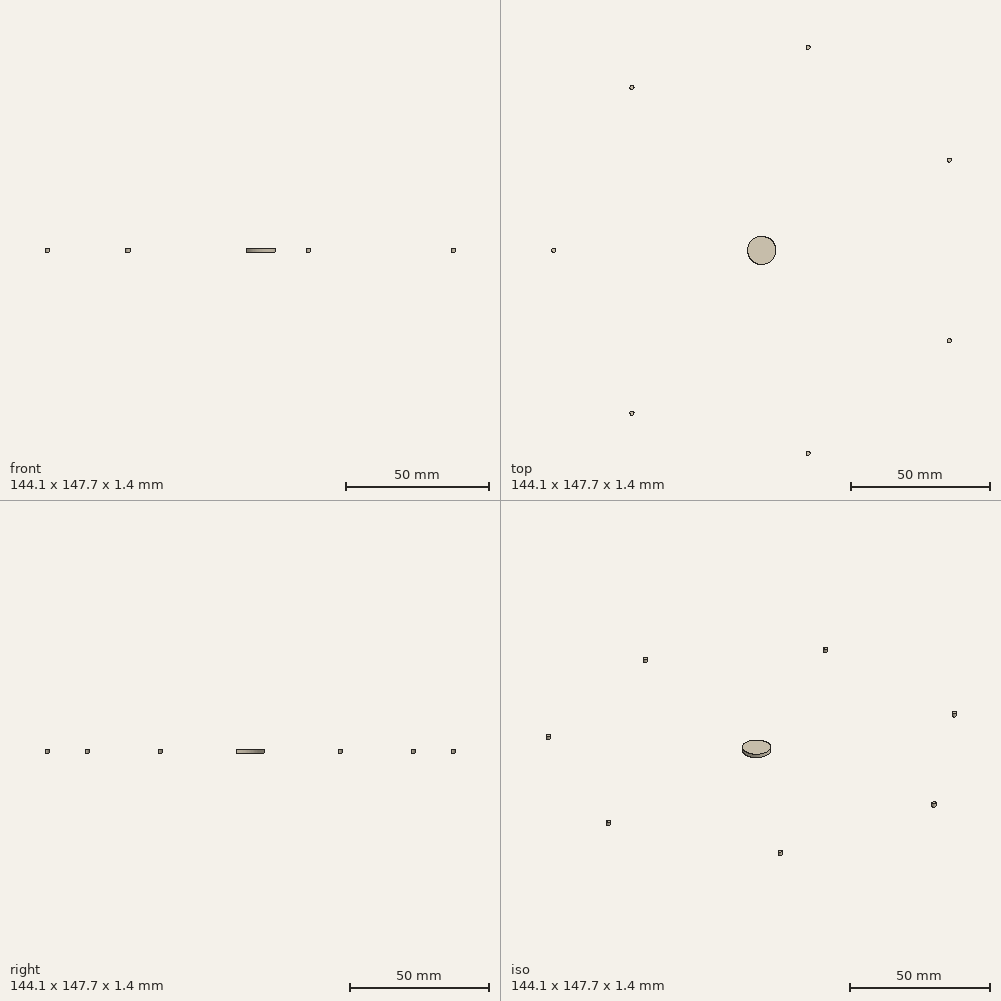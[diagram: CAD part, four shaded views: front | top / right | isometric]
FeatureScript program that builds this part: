
annotation { "Feature Type Name" : "Feature", "Feature Type Description" : "" }
export const myFeature = defineFeature(function(context is Context, id is Id, definition is map)
    precondition{}
    {
        {
            var Q0;
            Q0=qCreatedBy(makeId("Top.planeOp"),FACE);
            var sketch = newSketch(context, id + "F0", { "sketchPlane" : qUnion([Q0])});
            skLineSegment(sketch, "E0.0.left", {"start": v(-72.94, 1) * mm, "end": v(-5, 1) * mm});
            skLineSegment(sketch, "E0.0.right", {"start": v(-72.94, -1) * mm, "end": v(-5, -1) * mm});
            skCircle(sketch, "E1", {"center": v(-75, 0) * mm, "radius": 0.75 * mm});
            skArc(sketch, "E2", {"start": v(-74.31, 1.33) * mm, "mid": v(-76.5, 0) * mm, "end": v(-74.31, -1.33) * mm});
            skPoint(sketch, "E3.newPointA", {"position": v(-72.94, 1) * mm});
            skArc(sketch, "E3.filletArc", {"start": v(-74.31, 1.33) * mm, "mid": v(-73.65, 1.08) * mm, "end": v(-72.94, 1) * mm});
            skPoint(sketch, "E4.newPointB", {"position": v(-72.94, -1) * mm});
            skArc(sketch, "E4.filletArc", {"start": v(-72.94, -1) * mm, "mid": v(-73.65, -1.08) * mm, "end": v(-74.31, -1.33) * mm});
            skLineSegment(sketch, "E5.1.0", {"start": v(-46.26, -56.4) * mm, "end": v(-3.9, -3.29) * mm});
            skPoint(sketch, "E5.1.1", {"position": v(-44.7, -57.65) * mm});
            skPoint(sketch, "E5.1.2", {"position": v(-46.26, -56.4) * mm});
            skLineSegment(sketch, "E5.1.3", {"start": v(-44.7, -57.65) * mm, "end": v(-2.34, -4.53) * mm});
            skArc(sketch, "E5.1.4", {"start": v(-47.38, -57.27) * mm, "mid": v(-47.7, -59.81) * mm, "end": v(-45.3, -58.93) * mm});
            skCircle(sketch, "E5.1.5", {"center": v(-46.76, -58.64) * mm, "radius": 0.75 * mm});
            skArc(sketch, "E5.1.6", {"start": v(-44.7, -57.65) * mm, "mid": v(-45.07, -58.25) * mm, "end": v(-45.3, -58.93) * mm});
            skArc(sketch, "E5.1.7", {"start": v(-47.38, -57.27) * mm, "mid": v(-46.77, -56.9) * mm, "end": v(-46.26, -56.4) * mm});
            skLineSegment(sketch, "E5.2.0", {"start": v(15.26, -71.33) * mm, "end": v(0.14, -5.1) * mm});
            skPoint(sketch, "E5.2.1", {"position": v(17.2, -70.89) * mm});
            skPoint(sketch, "E5.2.2", {"position": v(15.26, -71.33) * mm});
            skLineSegment(sketch, "E5.2.3", {"start": v(17.2, -70.89) * mm, "end": v(2.09, -4.65) * mm});
            skArc(sketch, "E5.2.4", {"start": v(15.24, -72.75) * mm, "mid": v(17.02, -74.58) * mm, "end": v(17.84, -72.15) * mm});
            skCircle(sketch, "E5.2.5", {"center": v(16.69, -73.12) * mm, "radius": 0.75 * mm});
            skArc(sketch, "E5.2.6", {"start": v(17.2, -70.89) * mm, "mid": v(17.45, -71.56) * mm, "end": v(17.84, -72.15) * mm});
            skArc(sketch, "E5.2.7", {"start": v(15.24, -72.75) * mm, "mid": v(15.33, -72.04) * mm, "end": v(15.26, -71.33) * mm});
            skLineSegment(sketch, "E5.3.0", {"start": v(65.28, -32.55) * mm, "end": v(4.07, -3.07) * mm});
            skPoint(sketch, "E5.3.1", {"position": v(66.15, -30.75) * mm});
            skPoint(sketch, "E5.3.2", {"position": v(65.28, -32.55) * mm});
            skLineSegment(sketch, "E5.3.3", {"start": v(66.15, -30.75) * mm, "end": v(4.94, -1.27) * mm});
            skArc(sketch, "E5.3.4", {"start": v(66.38, -33.44) * mm, "mid": v(68.92, -33.2) * mm, "end": v(67.53, -31.04) * mm});
            skCircle(sketch, "E5.3.5", {"center": v(67.57, -32.54) * mm, "radius": 0.75 * mm});
            skArc(sketch, "E5.3.6", {"start": v(66.15, -30.75) * mm, "mid": v(66.82, -30.98) * mm, "end": v(67.53, -31.04) * mm});
            skArc(sketch, "E5.3.7", {"start": v(66.38, -33.44) * mm, "mid": v(65.88, -32.93) * mm, "end": v(65.28, -32.55) * mm});
            skLineSegment(sketch, "E5.4.0", {"start": v(66.15, 30.75) * mm, "end": v(4.94, 1.27) * mm});
            skPoint(sketch, "E5.4.1", {"position": v(65.28, 32.55) * mm});
            skPoint(sketch, "E5.4.2", {"position": v(66.15, 30.75) * mm});
            skLineSegment(sketch, "E5.4.3", {"start": v(65.28, 32.55) * mm, "end": v(4.07, 3.07) * mm});
            skArc(sketch, "E5.4.4", {"start": v(67.53, 31.04) * mm, "mid": v(68.92, 33.2) * mm, "end": v(66.38, 33.44) * mm});
            skCircle(sketch, "E5.4.5", {"center": v(67.57, 32.54) * mm, "radius": 0.75 * mm});
            skArc(sketch, "E5.4.6", {"start": v(65.28, 32.55) * mm, "mid": v(65.88, 32.93) * mm, "end": v(66.38, 33.44) * mm});
            skArc(sketch, "E5.4.7", {"start": v(67.53, 31.04) * mm, "mid": v(66.82, 30.98) * mm, "end": v(66.15, 30.75) * mm});
            skLineSegment(sketch, "E5.5.0", {"start": v(17.2, 70.89) * mm, "end": v(2.09, 4.65) * mm});
            skPoint(sketch, "E5.5.1", {"position": v(15.26, 71.33) * mm});
            skPoint(sketch, "E5.5.2", {"position": v(17.2, 70.89) * mm});
            skLineSegment(sketch, "E5.5.3", {"start": v(15.26, 71.33) * mm, "end": v(0.14, 5.1) * mm});
            skArc(sketch, "E5.5.4", {"start": v(17.84, 72.15) * mm, "mid": v(17.02, 74.58) * mm, "end": v(15.24, 72.75) * mm});
            skCircle(sketch, "E5.5.5", {"center": v(16.69, 73.12) * mm, "radius": 0.75 * mm});
            skArc(sketch, "E5.5.6", {"start": v(15.26, 71.33) * mm, "mid": v(15.33, 72.04) * mm, "end": v(15.24, 72.75) * mm});
            skArc(sketch, "E5.5.7", {"start": v(17.84, 72.15) * mm, "mid": v(17.45, 71.56) * mm, "end": v(17.2, 70.89) * mm});
            skLineSegment(sketch, "E5.6.0", {"start": v(-44.7, 57.65) * mm, "end": v(-2.34, 4.53) * mm});
            skPoint(sketch, "E5.6.1", {"position": v(-46.26, 56.4) * mm});
            skPoint(sketch, "E5.6.2", {"position": v(-44.7, 57.65) * mm});
            skLineSegment(sketch, "E5.6.3", {"start": v(-46.26, 56.4) * mm, "end": v(-3.9, 3.29) * mm});
            skArc(sketch, "E5.6.4", {"start": v(-45.3, 58.93) * mm, "mid": v(-47.7, 59.81) * mm, "end": v(-47.38, 57.27) * mm});
            skCircle(sketch, "E5.6.5", {"center": v(-46.76, 58.64) * mm, "radius": 0.75 * mm});
            skArc(sketch, "E5.6.6", {"start": v(-46.26, 56.4) * mm, "mid": v(-46.77, 56.9) * mm, "end": v(-47.38, 57.27) * mm});
            skArc(sketch, "E5.6.7", {"start": v(-45.3, 58.93) * mm, "mid": v(-45.07, 58.25) * mm, "end": v(-44.7, 57.65) * mm});
            skPoint(sketch, "E5.center", {"position": v(0, 0) * mm});
            skCircle(sketch, "E6", {"center": v(0, 0) * mm, "radius": 5.1 * mm});
            skSolve(sketch);
        }
        {
            var Q0;
            Q0 = qSketchRegion(id + "F0", true);
            extrude(context, id + "F1", {"entities" : qUnion([Q0]), "depth" : 1.4 * mm, "offsetDistance" : 25 * mm});
        }
    });
